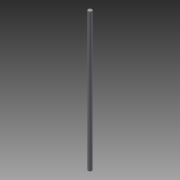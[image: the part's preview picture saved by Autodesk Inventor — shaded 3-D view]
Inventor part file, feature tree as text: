
AUTODESK INVENTOR PART (.ipt)
format: ipt  version: 2013 (Build 170138000, 138)  size: 60,416 bytes
history: native  units: in
note: dims shown in document units (in); Inventor stores cm internally (conversion verified against a paired STEP export)
features: extrude x1, sketch x1
ambient origin geometry x8: Origin, YZ Plane, XZ Plane, XY Plane, X Axis, Y Axis, Z Axis, Center Point
bodies: Solid1 (feature_tree)
feature tree (2):
  extrude  "Extrusion1"  Depth=18.75in TaperAngle=0.0deg
  sketch  "Sketch1"  dims[d0=0.5in d1=18.75in d2=0.0in]
